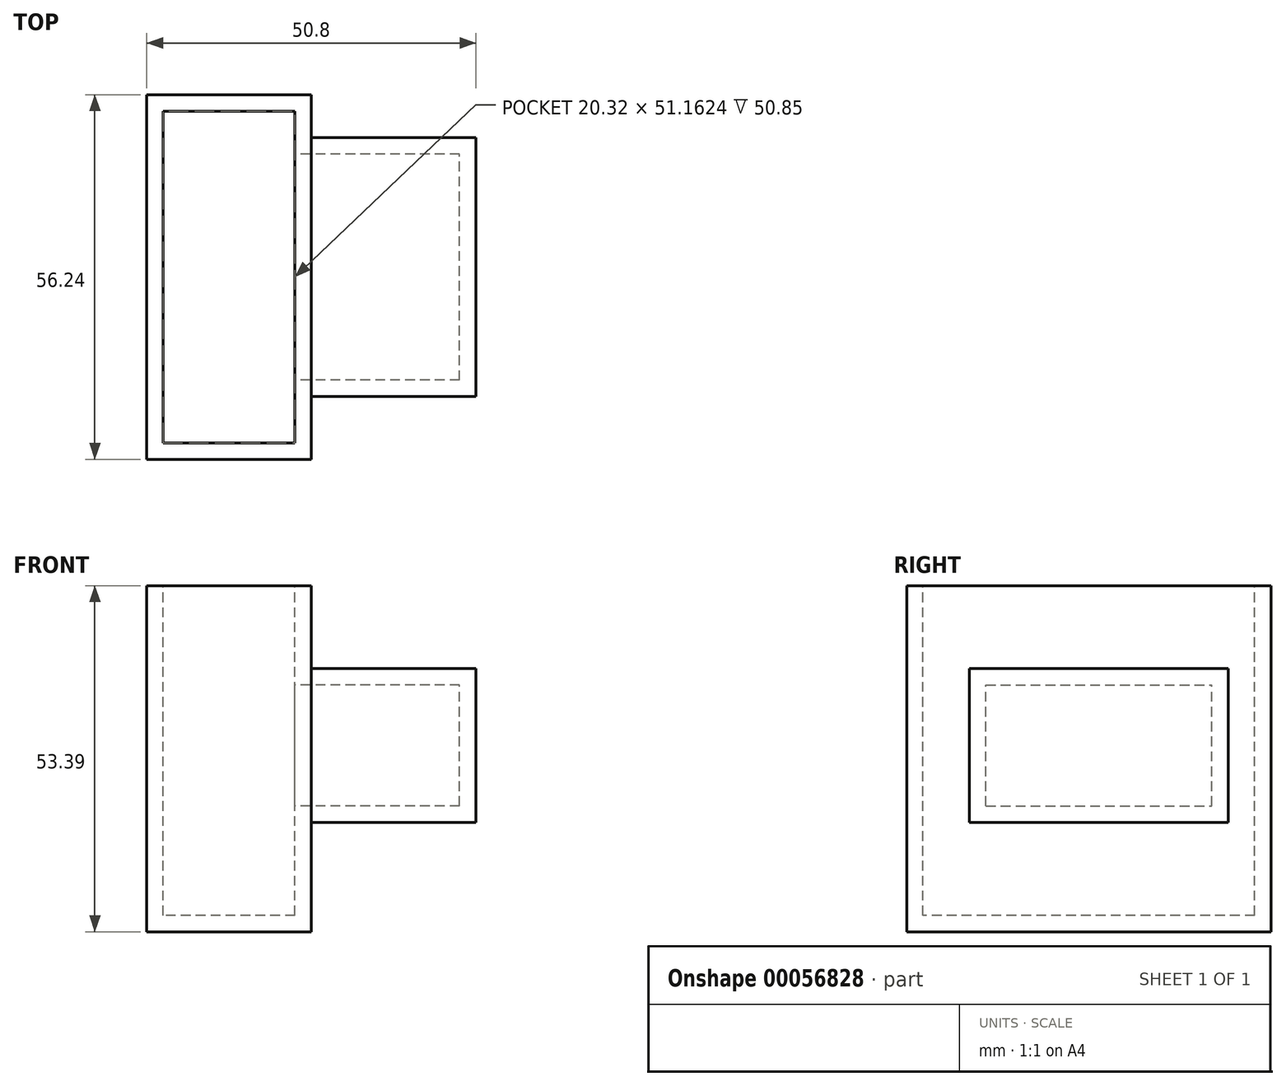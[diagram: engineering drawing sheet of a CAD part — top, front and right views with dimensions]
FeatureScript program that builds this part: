
annotation { "Feature Type Name" : "Feature", "Feature Type Description" : "" }
export const myFeature = defineFeature(function(context is Context, id is Id, definition is map)
    precondition{}
    {
        {
            var Q0;
            Q0=qCreatedBy(makeId("Top.planeOp"),FACE);
            var sketch = newSketch(context, id + "F0", { "sketchPlane" : qUnion([Q0])});
            skLineSegment(sketch, "E0.bottom", {"start": v(0, 0) * mm, "end": v(-35.9, 0) * mm});
            skLineSegment(sketch, "E0.top", {"start": v(0, 59.85) * mm, "end": v(-35.9, 59.85) * mm});
            skLineSegment(sketch, "E0.left", {"start": v(0, 0) * mm, "end": v(0, 59.85) * mm});
            skLineSegment(sketch, "E0.right", {"start": v(-35.9, 0) * mm, "end": v(-35.9, 59.85) * mm});
            skSolve(sketch);
        }
        {
            var Q0;
            Q0=makeQuery(id+"F0.imprint","IMPRINT",FACE,{"disambiguationData":[TD([[makeQuery(id+"F0.imprint","IMPRINT",EDGE,{"derivedFrom":sQuery(id+"F0.wireOp",EDGE,"E0.bottom")}),-1.0]])]});
            extrude(context, id + "F1", {"entities" : qUnion([Q0]), "depth" : 25.4 * mm});
        }
        {
            var Q0;
            Q0=qCreatedBy(makeId("Right.planeOp"),FACE);
            var sketch = newSketch(context, id + "F2", { "sketchPlane" : qUnion([Q0])});
            skLineSegment(sketch, "E1.bottom", {"start": v(0, 0) * mm, "end": v(-56.24, 0) * mm});
            skLineSegment(sketch, "E1.top", {"start": v(0, 53.4) * mm, "end": v(-56.24, 53.4) * mm});
            skLineSegment(sketch, "E1.left", {"start": v(0, 0) * mm, "end": v(0, 53.4) * mm});
            skLineSegment(sketch, "E1.right", {"start": v(-56.24, 0) * mm, "end": v(-56.24, 53.4) * mm});
            skSolve(sketch);
        }
        {
            var Q0;
            Q0=makeQuery(id+"F2.imprint","IMPRINT",FACE,{"disambiguationData":[TD([[makeQuery(id+"F2.imprint","IMPRINT",EDGE,{"derivedFrom":sQuery(id+"F2.wireOp",EDGE,"E1.bottom")}),-1.0]])]});
            extrude(context, id + "F3", {"entities" : qUnion([Q0]), "depth" : 25.4 * mm});
        }
        {
            var Q0;
            Q0=makeQuery(id+"F3.opExtrude","CAP_FACE",FACE,{"disambiguationData":[OSD([sQuery(id+"F2.wireOp",EDGE,"E1.bottom"),sQuery(id+"F2.wireOp",EDGE,"E1.top"),sQuery(id+"F2.wireOp",EDGE,"E1.left"),sQuery(id+"F2.wireOp",EDGE,"E1.right")])],"isStart":false});
            var sketch = newSketch(context, id + "F4", { "sketchPlane" : qUnion([Q0])});
            skLineSegment(sketch, "E2.bottom", {"start": v(-46.55, 16.87) * mm, "end": v(-6.6, 16.87) * mm});
            skLineSegment(sketch, "E2.top", {"start": v(-46.55, 40.62) * mm, "end": v(-6.6, 40.62) * mm});
            skLineSegment(sketch, "E2.left", {"start": v(-46.55, 16.87) * mm, "end": v(-46.55, 40.62) * mm});
            skLineSegment(sketch, "E2.right", {"start": v(-6.6, 16.87) * mm, "end": v(-6.6, 40.62) * mm});
            skSolve(sketch);
        }
        {
            var Q0;
            Q0=makeQuery(id+"F4.imprint","IMPRINT",FACE,{"disambiguationData":[TD([[makeQuery(id+"F4.imprint","IMPRINT",EDGE,{"derivedFrom":sQuery(id+"F4.wireOp",EDGE,"E2.bottom")}),1.0]])]});
            extrude(context, id + "F5", {"entities" : qUnion([Q0]), "operationType" : NewBodyOperationType.ADD, "depth" : 25.4 * mm});
        }
        {
            var Q0;
            Q0=makeQuery(id+"F3.opExtrude","SWEPT_FACE",FACE,{"disambiguationData":[OSD([sQuery(id+"F2.wireOp",EDGE,"E1.top")])]});
            shell(context, id + "F6", {"entities" : qUnion([Q0]), "thickness" : 2.54 * mm});
        }
        {
            var Q0;
            Q0=makeQuery(id+"F1.opExtrude","SWEPT_BODY",BODY,{"disambiguationData":[OSD([sQuery(id+"F0.wireOp",EDGE,"E0.bottom"),sQuery(id+"F0.wireOp",EDGE,"E0.top"),sQuery(id+"F0.wireOp",EDGE,"E0.left"),sQuery(id+"F0.wireOp",EDGE,"E0.right")])]});
            deleteBodies(context, id + "F7", {"entities" : qUnion([Q0])});
        }
    });
